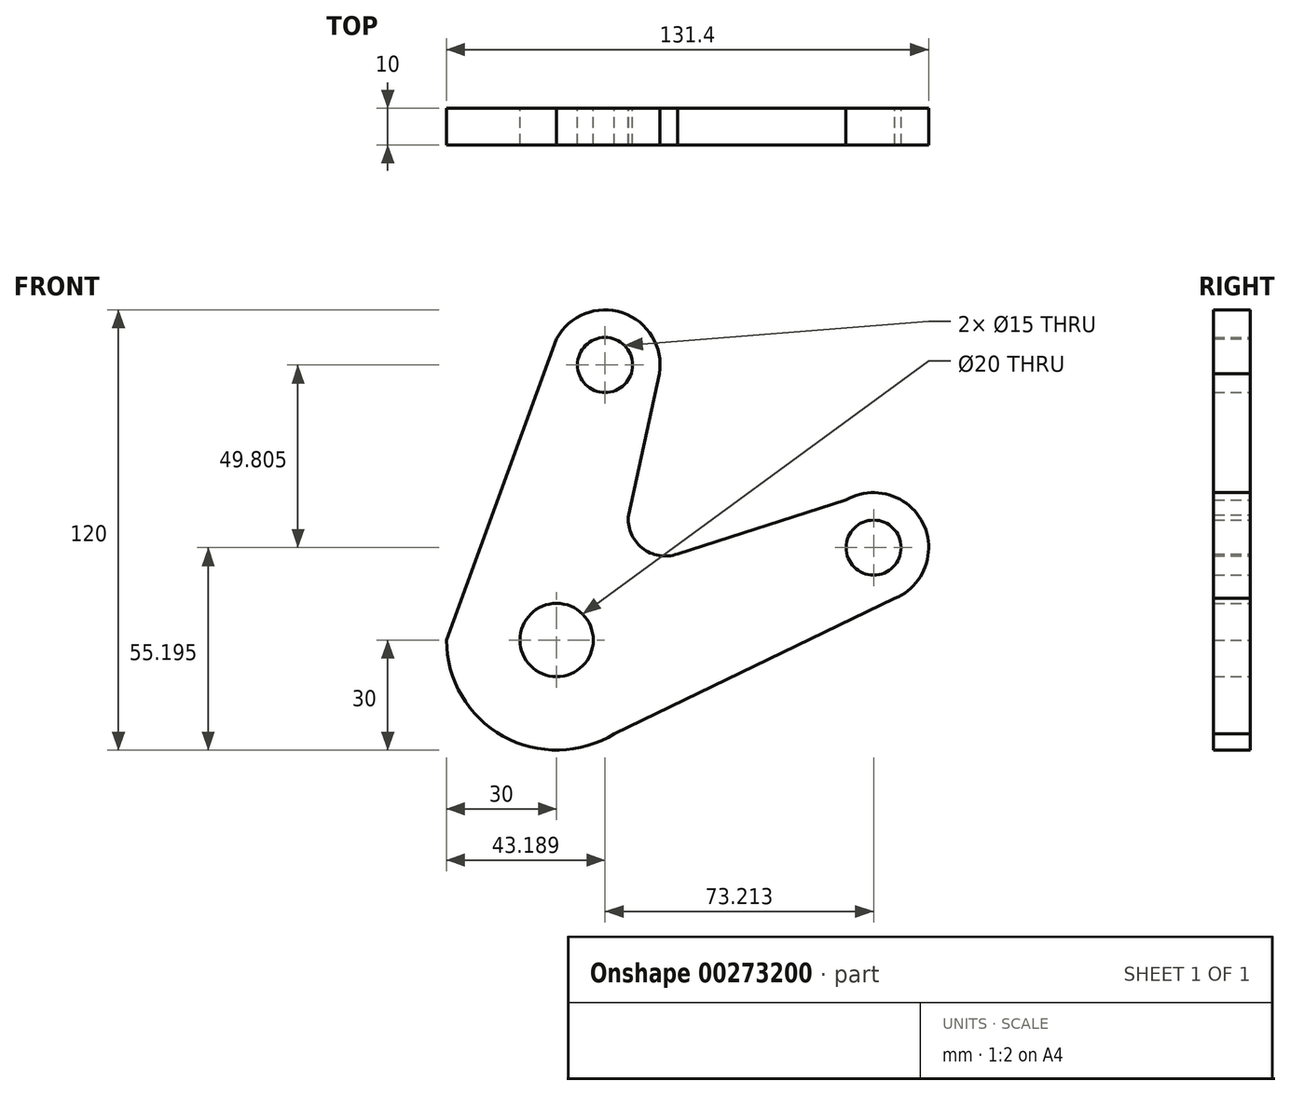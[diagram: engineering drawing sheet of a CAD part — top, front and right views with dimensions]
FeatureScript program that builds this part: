
annotation { "Feature Type Name" : "Feature", "Feature Type Description" : "" }
export const myFeature = defineFeature(function(context is Context, id is Id, definition is map)
    precondition{}
    {
        {
            var Q0;
            Q0=qCreatedBy(makeId("Front.planeOp"),FACE);
            var sketch = newSketch(context, id + "F0", { "sketchPlane" : qUnion([Q0])});
            skCircle(sketch, "E0", {"center": v(0, 0) * mm, "radius": 10 * mm});
            skCircle(sketch, "E1", {"center": v(13.19, 75) * mm, "radius": 7.5 * mm});
            skCircle(sketch, "E2", {"center": v(86.4, 25.2) * mm, "radius": 7.5 * mm});
            skArc(sketch, "E3", {"start": v(-30, 0) * mm, "mid": v(-14.61, -26.2) * mm, "end": v(15.76, -25.53) * mm});
            skArc(sketch, "E4", {"start": v(28, 72.65) * mm, "mid": v(18, 89.2) * mm, "end": v(0, 82.15) * mm});
            skArc(sketch, "E5", {"start": v(92.2, 11.36) * mm, "mid": v(99.84, 31.87) * mm, "end": v(78.88, 38.17) * mm});
            skArc(sketch, "E6", {"start": v(19.64, 34.16) * mm, "mid": v(23.29, 25.1) * mm, "end": v(32.92, 23.48) * mm});
            skLineSegment(sketch, "E7", {"start": v(19.64, 34.16) * mm, "end": v(28, 72.65) * mm});
            skLineSegment(sketch, "E8", {"start": v(78.88, 38.17) * mm, "end": v(32.92, 23.48) * mm});
            skLineSegment(sketch, "E9", {"start": v(0, 82.15) * mm, "end": v(-30, 0) * mm});
            skLineSegment(sketch, "E10", {"start": v(15.76, -25.53) * mm, "end": v(92.2, 11.36) * mm});
            skSolve(sketch);
        }
        {
            var Q0;
            Q0 = qSketchRegion(id + "F0", true);
            extrude(context, id + "F1", {"entities" : qUnion([Q0]), "depth" : 10 * mm});
        }
    });
